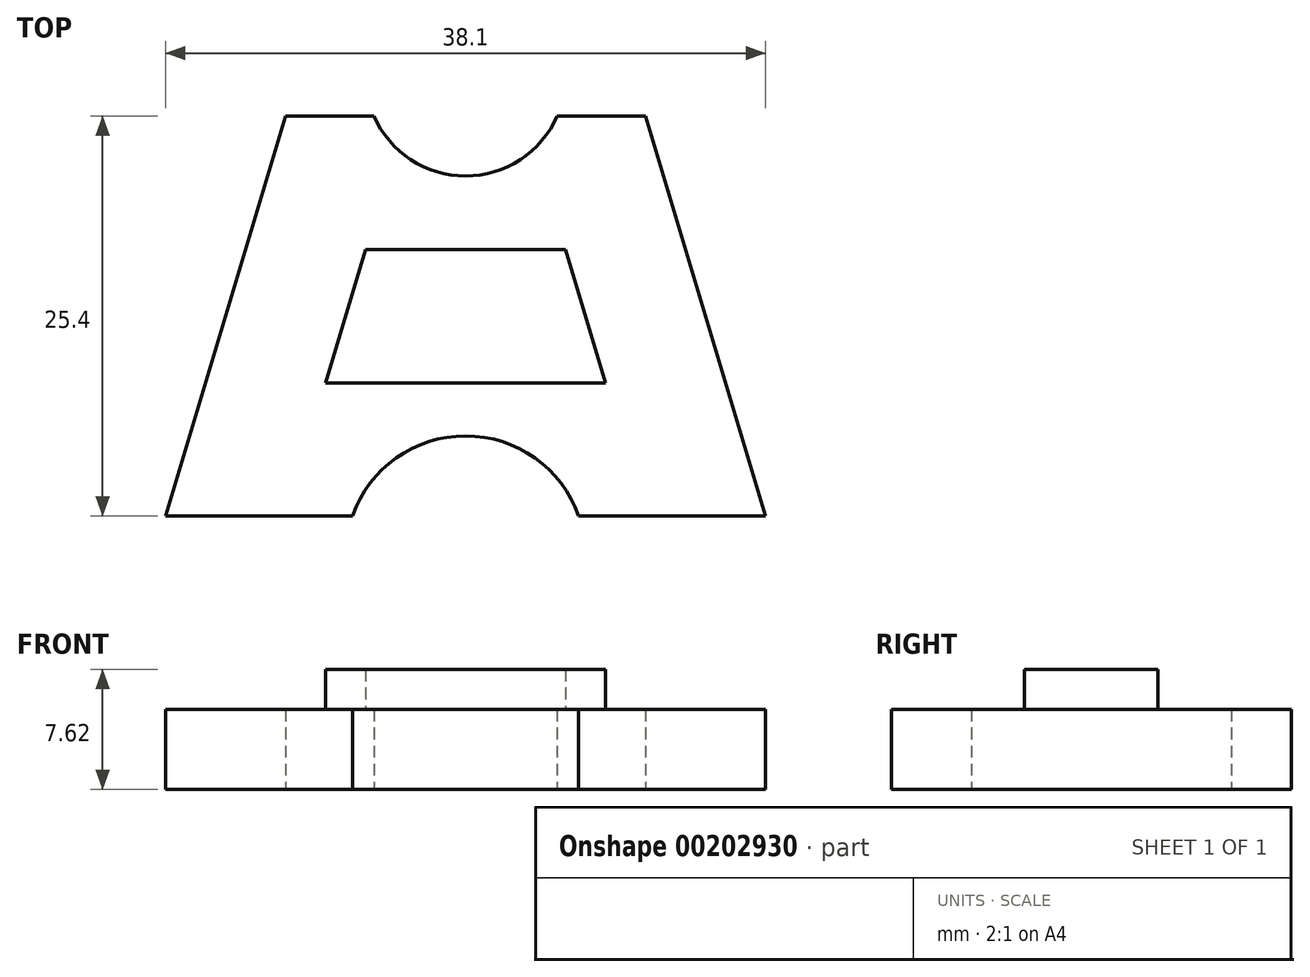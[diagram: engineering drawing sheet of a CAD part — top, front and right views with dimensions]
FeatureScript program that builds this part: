
annotation { "Feature Type Name" : "Feature", "Feature Type Description" : "" }
export const myFeature = defineFeature(function(context is Context, id is Id, definition is map)
    precondition{}
    {
        {
            var Q0;
            Q0=qCreatedBy(makeId("Top.planeOp"),FACE);
            var sketch = newSketch(context, id + "F0", { "sketchPlane" : qUnion([Q0])});
            skLineSegment(sketch, "E0.bottom", {"start": v(0, 0) * mm, "end": v(38.1, 0) * mm});
            skLineSegment(sketch, "E1", {"start": v(0, 0) * mm, "end": v(7.62, 25.4) * mm});
            skLineSegment(sketch, "E2", {"start": v(30.48, 25.4) * mm, "end": v(38.1, 0) * mm});
            skPoint(sketch, "E3", {"position": v(19.05, 0) * mm});
            skLineSegment(sketch, "E4", {"start": v(10.16, 8.46) * mm, "end": v(12.7, 16.92) * mm});
            skLineSegment(sketch, "E5", {"start": v(12.7, 16.92) * mm, "end": v(25.4, 16.92) * mm});
            skLineSegment(sketch, "E6", {"start": v(25.4, 16.92) * mm, "end": v(27.94, 8.46) * mm});
            skLineSegment(sketch, "E7", {"start": v(27.94, 8.46) * mm, "end": v(10.16, 8.46) * mm});
            skPoint(sketch, "E8", {"position": v(19.05, 16.92) * mm});
            skPoint(sketch, "E9", {"position": v(19.05, 8.46) * mm});
            skLineSegment(sketch, "E10", {"start": v(7.62, 25.4) * mm, "end": v(30.48, 25.4) * mm});
            skPoint(sketch, "E11", {"position": v(19.05, 25.4) * mm});
            skPoint(sketch, "E12", {"position": v(19.05, -2.54) * mm});
            skPoint(sketch, "E13", {"position": v(19.05, 27.94) * mm});
            skSolve(sketch);
        }
        {
            var Q0;
            {var subQ0=sQuery(id+"F0.wireOp",EDGE,"E1");Q0=makeQuery(id+"F0.imprint","IMPRINT",FACE,{"disambiguationData":[TD([[makeQuery(id+"F0.imprint","IMPRINT",EDGE,{"derivedFrom":subQ0}),-1.0]])]});}
            var Q1;
            Q1=makeQuery(id+"F0.imprint","IMPRINT",FACE,{"disambiguationData":[TD([[makeQuery(id+"F0.imprint","IMPRINT",EDGE,{"derivedFrom":sQuery(id+"F0.wireOp",EDGE,"E4")}),-1.0]])]});
            extrude(context, id + "F1", {"entities" : qUnion([Q0, Q1]), "depth" : 5.08 * mm});
        }
        {
            var Q0;
            Q0=makeQuery(id+"F0.imprint","IMPRINT",FACE,{"disambiguationData":[TD([[makeQuery(id+"F0.imprint","IMPRINT",EDGE,{"derivedFrom":sQuery(id+"F0.wireOp",EDGE,"E4")}),-1.0]])]});
            extrude(context, id + "F2", {"entities" : qUnion([Q0]), "operationType" : NewBodyOperationType.ADD, "depth" : 7.62 * mm});
        }
        {
            var Q0;
            Q0=sQuery(id+"F0.wireOp",VERTEX,"E12");
            var Q1;
            Q1=makeQuery(id+"F1.opExtrude","SWEPT_BODY",BODY,{"disambiguationData":[OSD([sQuery(id+"F0.wireOp",EDGE,"E0.bottom"),sQuery(id+"F0.wireOp",EDGE,"E1"),sQuery(id+"F0.wireOp",EDGE,"E2"),sQuery(id+"F0.wireOp",EDGE,"E10")])]});
            hole(context, id + "F3", {"style" : HoleStyle.SIMPLE, "endStyle" : HoleEndStyle.THROUGH, "oppositeDirection" : true, "holeDiameter" : 15.24 * mm, "locations" : qUnion([Q0]), "scope" : qUnion([Q1]), "isTappedThrough" : true});
        }
        {
            var Q0;
            Q0=sQuery(id+"F0.wireOp",VERTEX,"E13");
            var Q1;
            Q1=makeQuery(id+"F1.opExtrude","SWEPT_BODY",BODY,{"disambiguationData":[OSD([sQuery(id+"F0.wireOp",EDGE,"E0.bottom"),sQuery(id+"F0.wireOp",EDGE,"E1"),sQuery(id+"F0.wireOp",EDGE,"E2"),sQuery(id+"F0.wireOp",EDGE,"E10")])]});
            hole(context, id + "F4", {"style" : HoleStyle.SIMPLE, "endStyle" : HoleEndStyle.THROUGH, "oppositeDirection" : true, "holeDiameter" : 12.7 * mm, "locations" : qUnion([Q0]), "scope" : qUnion([Q1]), "isTappedThrough" : true});
        }
    });
